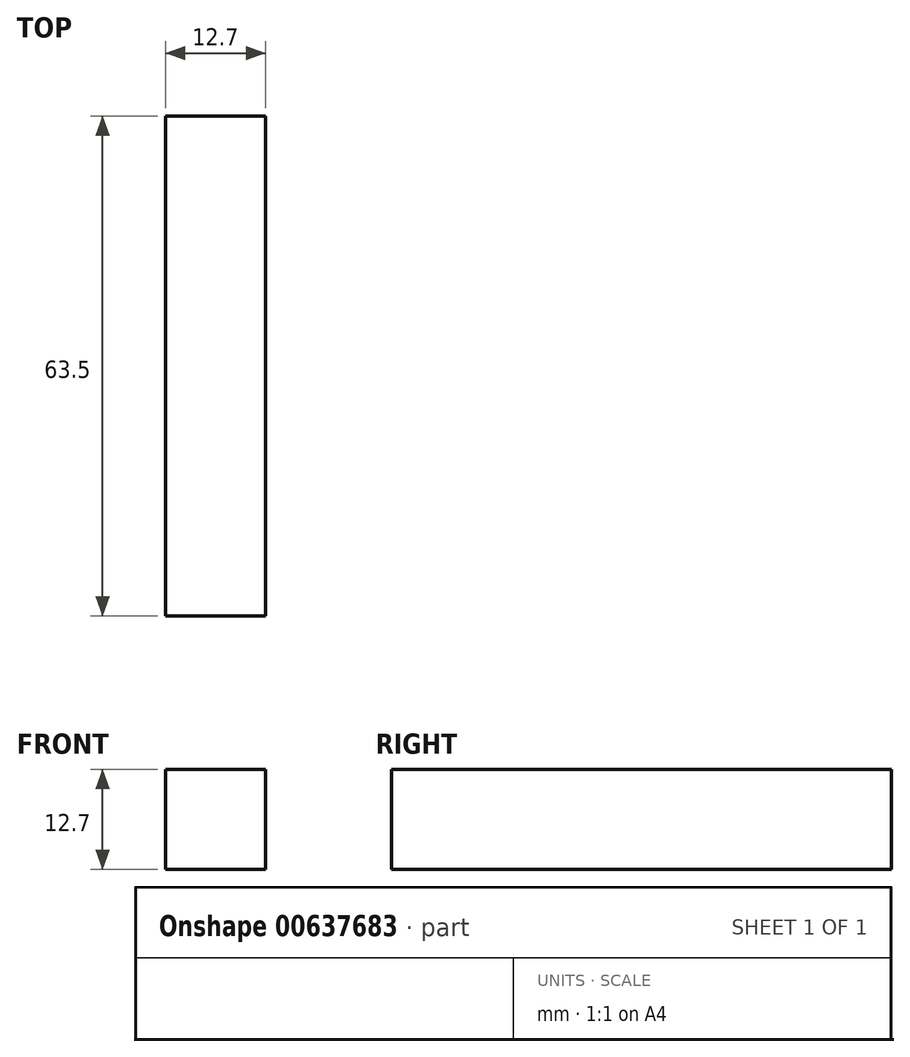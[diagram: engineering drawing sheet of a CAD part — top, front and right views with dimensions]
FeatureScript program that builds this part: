
annotation { "Feature Type Name" : "Feature", "Feature Type Description" : "" }
export const myFeature = defineFeature(function(context is Context, id is Id, definition is map)
    precondition{}
    {
        {
            var Q0;
            Q0=qCreatedBy(makeId("Top.planeOp"),FACE);
            var sketch = newSketch(context, id + "F0", { "sketchPlane" : qUnion([Q0])});
            skLineSegment(sketch, "E0.bottom", {"start": v(6.35, 31.75) * mm, "end": v(-6.35, 31.75) * mm});
            skLineSegment(sketch, "E0.top", {"start": v(6.35, -31.75) * mm, "end": v(-6.35, -31.75) * mm});
            skLineSegment(sketch, "E0.left", {"start": v(6.35, 31.75) * mm, "end": v(6.35, -31.75) * mm});
            skLineSegment(sketch, "E0.right", {"start": v(-6.35, 31.75) * mm, "end": v(-6.35, -31.75) * mm});
            skPoint(sketch, "E0.middle", {"position": v(0, 0) * mm});
            skSolve(sketch);
        }
        {
            var Q0;
            Q0=makeQuery(id+"F0.imprint","IMPRINT",FACE,{"disambiguationData":[TD([[makeQuery(id+"F0.imprint","IMPRINT",EDGE,{"derivedFrom":sQuery(id+"F0.wireOp",EDGE,"E0.bottom")}),1.0]])]});
            extrude(context, id + "F1", {"entities" : qUnion([Q0]), "depth" : 12.7 * mm, "offsetDistance" : 25 * mm});
        }
    });
